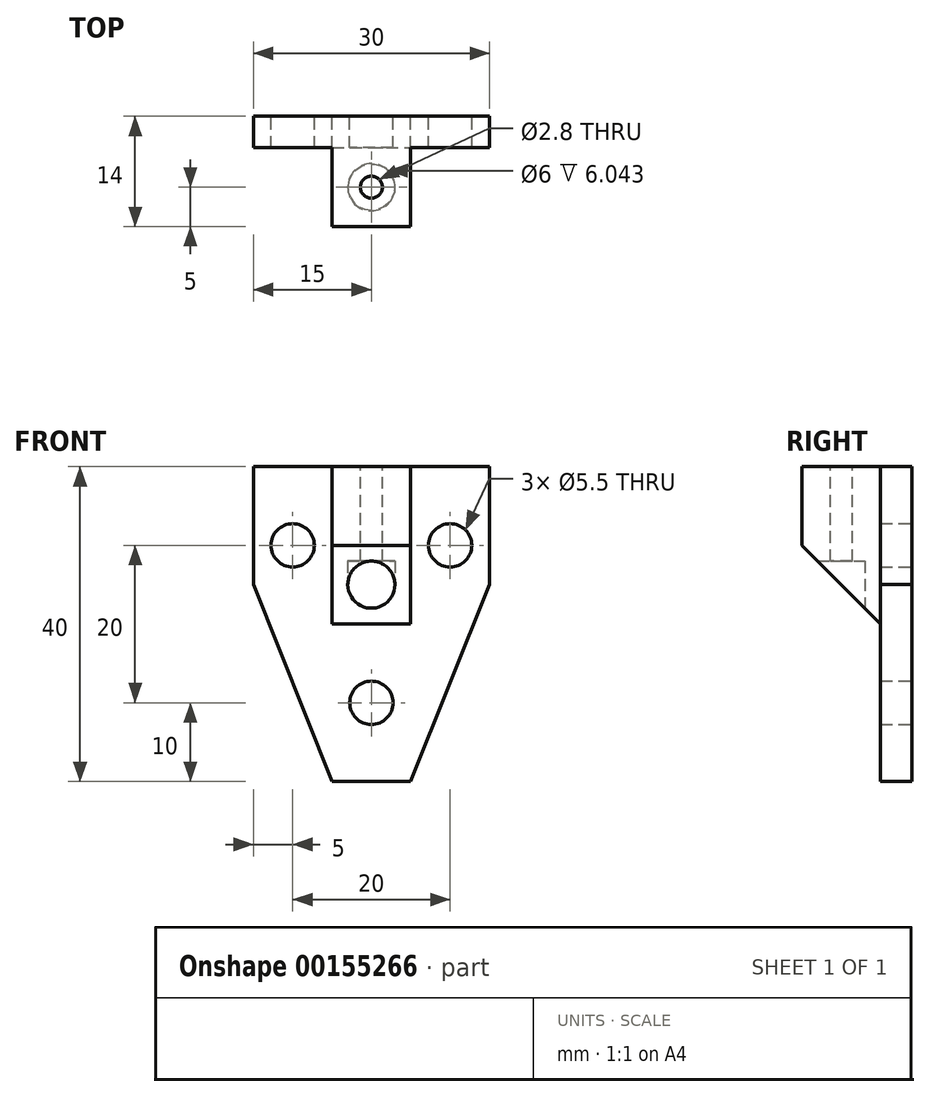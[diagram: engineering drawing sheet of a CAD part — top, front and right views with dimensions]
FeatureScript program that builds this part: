
annotation { "Feature Type Name" : "Feature", "Feature Type Description" : "" }
export const myFeature = defineFeature(function(context is Context, id is Id, definition is map)
    precondition{}
    {
        {
            var Q0;
            Q0=qCreatedBy(makeId("Front.planeOp"),FACE);
            var sketch = newSketch(context, id + "F0", { "sketchPlane" : qUnion([Q0])});
            skLineSegment(sketch, "E0", {"start": v(-32.16, 10) * mm, "end": v(45.14, 10) * mm, "construction": true});
            skCircle(sketch, "E1", {"center": v(-10, 10) * mm, "radius": 2.75 * mm});
            skCircle(sketch, "E2", {"center": v(10, 10) * mm, "radius": 2.75 * mm});
            skCircle(sketch, "E3", {"center": v(0, -10) * mm, "radius": 2.75 * mm});
            skLineSegment(sketch, "E4", {"start": v(0, 20) * mm, "end": v(15, 20) * mm});
            skLineSegment(sketch, "E5", {"start": v(15, 20) * mm, "end": v(15, 5) * mm});
            skLineSegment(sketch, "E6", {"start": v(15, 5) * mm, "end": v(5, -20) * mm});
            skLineSegment(sketch, "E7", {"start": v(5, -20) * mm, "end": v(0, -20) * mm});
            skLineSegment(sketch, "E8.MirrorCS", {"start": v(0, 20) * mm, "end": v(-15, 20) * mm});
            skLineSegment(sketch, "E9.MirrorCS", {"start": v(-15, 20) * mm, "end": v(-15, 5) * mm});
            skLineSegment(sketch, "E10.MirrorCS", {"start": v(-5, -20) * mm, "end": v(0, -20) * mm});
            skLineSegment(sketch, "E11.MirrorCS", {"start": v(-15, 5) * mm, "end": v(-5, -20) * mm});
            skSolve(sketch);
        }
        {
            var Q0;
            Q0 = qSketchRegion(id + "F0", true);
            extrude(context, id + "F1", {"entities" : qUnion([Q0]), "depth" : 4 * mm});
        }
        {
            var Q0;
            Q0=makeQuery(id+"F1.opExtrude","CAP_FACE",FACE,{"disambiguationData":[OSD([sQuery(id+"F0.wireOp",EDGE,"E1"),sQuery(id+"F0.wireOp",EDGE,"E2"),sQuery(id+"F0.wireOp",EDGE,"E3"),sQuery(id+"F0.wireOp",EDGE,"E4"),sQuery(id+"F0.wireOp",EDGE,"E5"),sQuery(id+"F0.wireOp",EDGE,"E6"),sQuery(id+"F0.wireOp",EDGE,"E7"),sQuery(id+"F0.wireOp",EDGE,"E8.MirrorCS"),sQuery(id+"F0.wireOp",EDGE,"E9.MirrorCS"),sQuery(id+"F0.wireOp",EDGE,"E10.MirrorCS"),sQuery(id+"F0.wireOp",EDGE,"E11.MirrorCS")])],"isStart":false});
            var sketch = newSketch(context, id + "F2", { "sketchPlane" : qUnion([Q0])});
            skLineSegment(sketch, "E12.bottom", {"start": v(-5, 20) * mm, "end": v(5, 20) * mm});
            skLineSegment(sketch, "E12.top", {"start": v(-5, 0) * mm, "end": v(5, 0) * mm});
            skLineSegment(sketch, "E12.left", {"start": v(-5, 20) * mm, "end": v(-5, 0) * mm});
            skLineSegment(sketch, "E12.right", {"start": v(5, 20) * mm, "end": v(5, 0) * mm});
            skSolve(sketch);
        }
        {
            var Q0;
            Q0 = qSketchRegion(id + "F2", true);
            extrude(context, id + "F3", {"entities" : qUnion([Q0]), "operationType" : NewBodyOperationType.ADD, "depth" : 10 * mm});
        }
        {
            var Q0;
            Q0=makeQuery(id+"F3.opExtrude","CAP_EDGE",EDGE,{"disambiguationData":[OSD([sQuery(id+"F2.wireOp",EDGE,"E12.top")])],"isStart":false});
            chamfer(context, id + "F4", {"entities" : qUnion([Q0]), "width" : 10 * mm, "tangentPropagation" : true});
        }
        {
            var Q0;
            Q0=makeQuery(id+"F3.boolean.opBoolean","MERGE",FACE,{"derivedFrom":[makeQuery(id+"F1.opExtrude","SWEPT_FACE",FACE,{"disambiguationData":[OSD([sQuery(id+"F0.wireOp",EDGE,"E4"),sQuery(id+"F0.wireOp",EDGE,"E8.MirrorCS")])]}),makeQuery(id+"F3.opExtrude","SWEPT_FACE",FACE,{"disambiguationData":[OSD([sQuery(id+"F2.wireOp",EDGE,"E12.bottom")])]})]});
            var sketch = newSketch(context, id + "F5", { "sketchPlane" : qUnion([Q0])});
            skLineSegment(sketch, "E13", {"start": v(0, -14) * mm, "end": v(0, 0) * mm, "construction": true});
            skCircle(sketch, "E14", {"center": v(0, -9) * mm, "radius": 1.4 * mm});
            skSolve(sketch);
        }
        {
            var Q0;
            Q0 = qSketchRegion(id + "F5", true);
            extrude(context, id + "F6", {"entities" : qUnion([Q0]), "operationType" : NewBodyOperationType.REMOVE, "oppositeDirection" : true, "depth" : 25 * mm});
        }
        {
            var Q0;
            Q0=qCreatedBy(makeId("Top.planeOp"),FACE);
            var sketch = newSketch(context, id + "F7", { "sketchPlane" : qUnion([Q0])});
            skCircle(sketch, "E15", {"center": v(0, -9) * mm, "radius": 3 * mm});
            skSolve(sketch);
        }
        {
            var Q0;
            Q0 = qSketchRegion(id + "F7", true);
            extrude(context, id + "F8", {"entities" : qUnion([Q0]), "operationType" : NewBodyOperationType.REMOVE, "depth" : 8 * mm});
        }
    });
